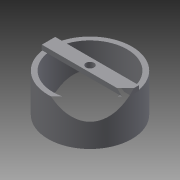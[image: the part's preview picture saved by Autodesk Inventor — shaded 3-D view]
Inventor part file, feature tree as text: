
AUTODESK INVENTOR PART (.ipt)
format: ipt  version: 2014 SP2 (Build 180246200, 246)  size: 156,672 bytes
history: native  units: mm
features: sketch x3, extrude x2, hole x1, reference x1
ambient origin geometry x8: Origin, YZ Plane, XZ Plane, XY Plane, X Axis, Y Axis, Z Axis, Center Point
bodies: Solid1 (feature_tree)
feature tree (7):
  extrude  "Extrusion1"  Depth=6.5mm
  extrude  "Extrusion5"  Depth=14.0mm
  hole  "Hole1"  [1 undecoded]
  sketch  "Sketch1"  dims[d0=1.5mm d1=6.5mm]
  reference  "Reference1"
  sketch  "Sketch5"  dims[d2=40.0mm d3=0.0mm d27=14.0mm]
  sketch  "Sketch6"  dims[d28=5.0mm d29=0.0mm d30=8.5mm d31=6.0mm d32=4.0mm d33=2.0mm d34=90.0deg d35=8.0mm d36=20.594885mm]
note: 1 required parameter value undecoded (feature->parameter linkage not recoverable at this tier; creation-order binding heuristic only, values carry confidence <= 0.55)
